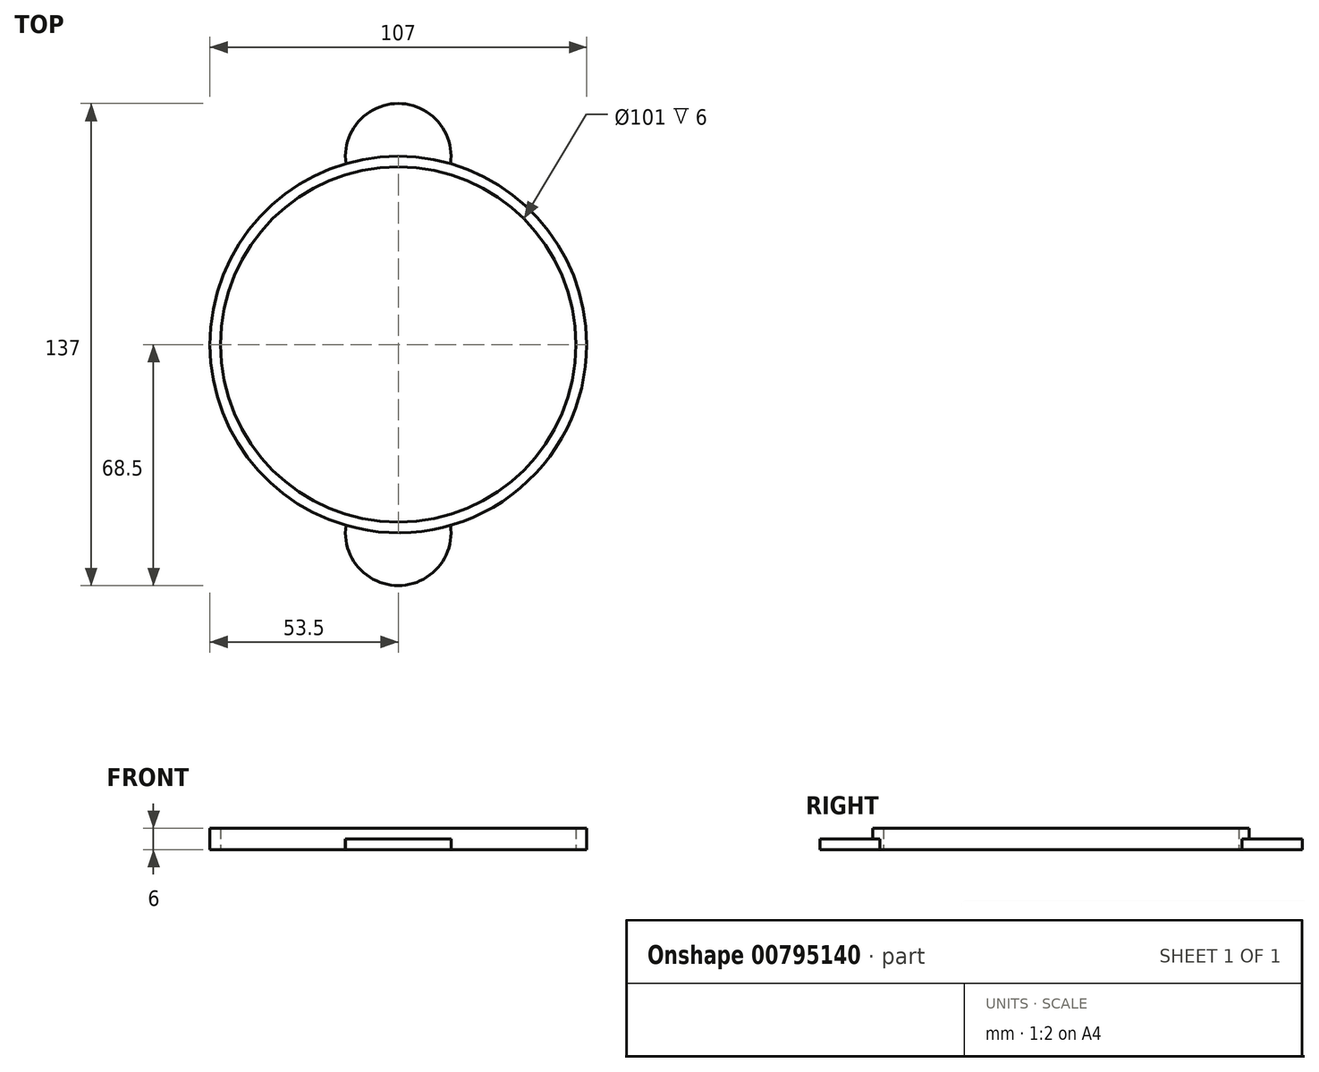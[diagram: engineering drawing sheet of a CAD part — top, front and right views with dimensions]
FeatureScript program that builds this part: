
annotation { "Feature Type Name" : "Feature", "Feature Type Description" : "" }
export const myFeature = defineFeature(function(context is Context, id is Id, definition is map)
    precondition{}
    {
        {
            var Q0;
            Q0=qCreatedBy(makeId("Top.planeOp"),FACE);
            var sketch = newSketch(context, id + "F0", { "sketchPlane" : qUnion([Q0])});
            skCircle(sketch, "E0", {"center": v(0, 0) * mm, "radius": 19.1 * mm, "construction": true});
            skCircle(sketch, "E1", {"center": v(20.6, 0) * mm, "radius": 1.5 * mm, "construction": true});
            skCircle(sketch, "E2", {"center": v(20.6, 0) * mm, "radius": 29.9 * mm, "construction": true});
            skCircle(sketch, "E3", {"center": v(0, 0) * mm, "radius": 50.5 * mm});
            skCircle(sketch, "E4.0", {"center": v(0, 0) * mm, "radius": 53.5 * mm});
            skSolve(sketch);
        }
        {
            var Q0;
            Q0 = qSketchRegion(id + "F0", true);
            extrude(context, id + "F1", {"entities" : qUnion([Q0]), "depth" : 6 * mm, "offsetDistance" : 25 * mm});
        }
        {
            var Q0;
            Q0=qCreatedBy(makeId("Top.planeOp"),FACE);
            var sketch = newSketch(context, id + "F2", { "sketchPlane" : qUnion([Q0])});
            skArc(sketch, "E5.0", {"start": v(-14.85, -51.4) * mm, "mid": v(0, -53.5) * mm, "end": v(14.85, -51.4) * mm});
            skArc(sketch, "E6", {"start": v(14.85, 51.4) * mm, "mid": v(0, 68.5) * mm, "end": v(-14.85, 51.4) * mm});
            skArc(sketch, "E7", {"start": v(-14.85, -51.4) * mm, "mid": v(0, -68.5) * mm, "end": v(14.85, -51.4) * mm});
            skArc(sketch, "E8.trimOffspring", {"start": v(14.85, 51.4) * mm, "mid": v(0, 53.5) * mm, "end": v(-14.85, 51.4) * mm});
            skSolve(sketch);
        }
        {
            var Q0;
            Q0 = qSketchRegion(id + "F2", true);
            extrude(context, id + "F3", {"entities" : qUnion([Q0]), "operationType" : NewBodyOperationType.ADD, "depth" : 3 * mm, "offsetDistance" : 25 * mm});
        }
    });
